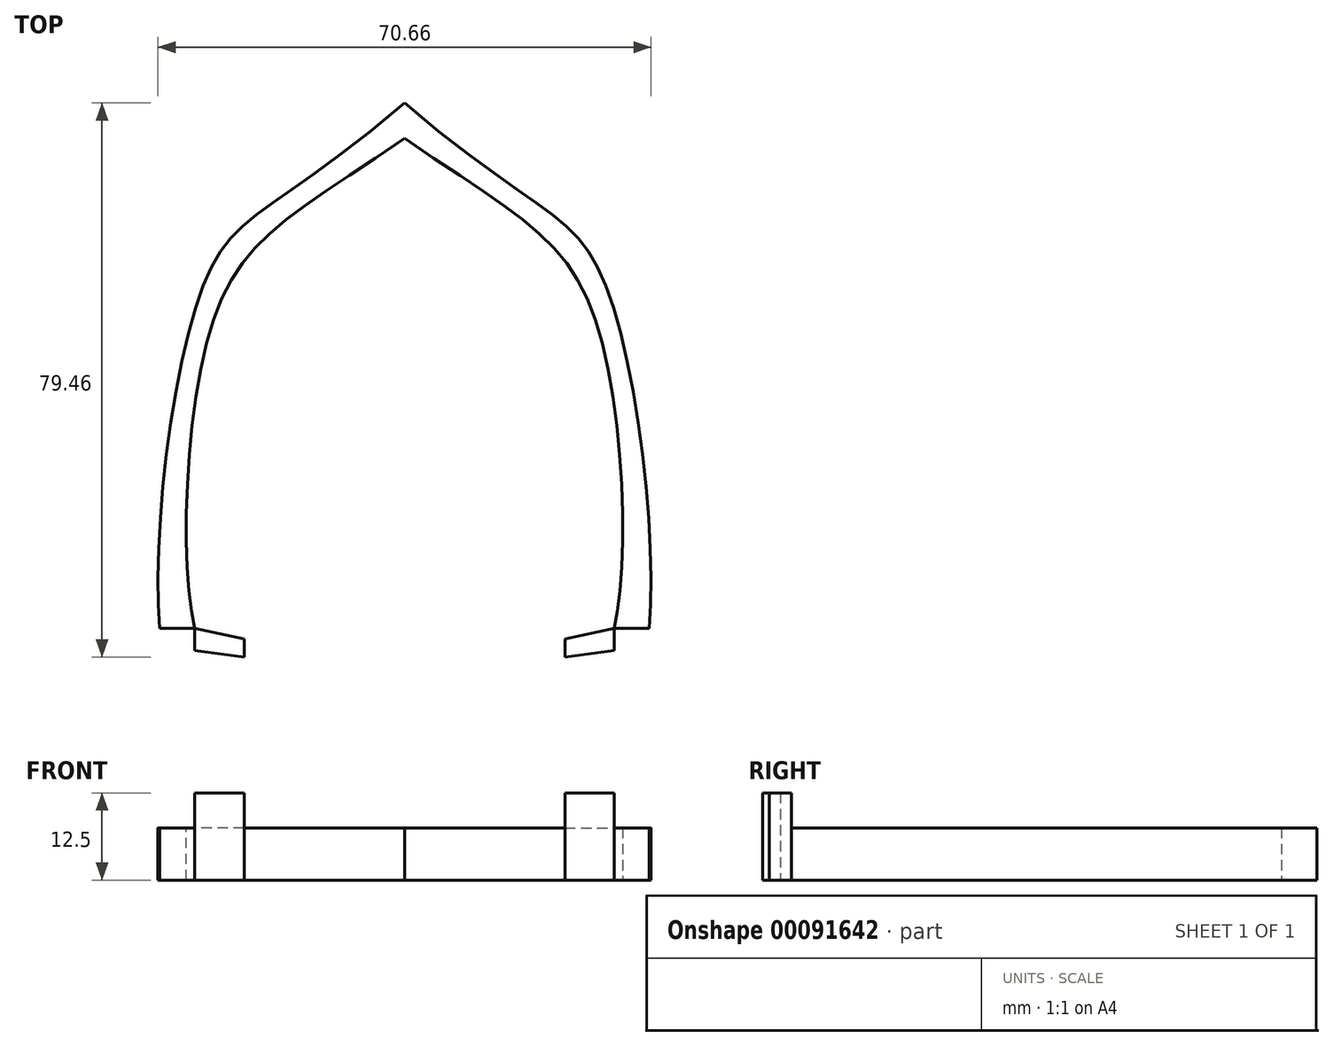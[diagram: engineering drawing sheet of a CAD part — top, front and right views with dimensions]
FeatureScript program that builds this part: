
annotation { "Feature Type Name" : "Feature", "Feature Type Description" : "" }
export const myFeature = defineFeature(function(context is Context, id is Id, definition is map)
    precondition{}
    {
        {
            var Q0;
            Q0=qCreatedBy(makeId("Top.planeOp"),FACE);
            var sketch = newSketch(context, id + "F0", { "sketchPlane" : qUnion([Q0])});
            skFitSpline(sketch, "E0", {"points": [v(0, 53.23) * mm, v(-28.51, 27.9) * mm, v(-35.06, -22.11) * mm], "startDerivative": vector(-121.37, -103.36) * mm, "endDerivative": vector(6.7, -73.45) * mm});
            skLineSegment(sketch, "E1", {"start": v(0, 53.23) * mm, "end": v(0, 48.14) * mm});
            skFitSpline(sketch, "E2", {"points": [v(0, 48.14) * mm, v(-27.4, 22.06) * mm, v(-30.06, -22.11) * mm], "startDerivative": vector(-100.93, -68.6) * mm, "endDerivative": vector(12.09, -49.62) * mm});
            skLineSegment(sketch, "E3", {"start": v(-30.06, -22.11) * mm, "end": v(-35.06, -22.11) * mm});
            skLineSegment(sketch, "E4.left", {"start": v(-30.06, -22.11) * mm, "end": v(-30.06, -27.16) * mm});
            skLineSegment(sketch, "E5.bottom", {"start": v(-35.06, -22.11) * mm, "end": v(-30.06, -22.11) * mm});
            skLineSegment(sketch, "E6", {"start": v(-30.06, -22.11) * mm, "end": v(-22.99, -23.66) * mm});
            skLineSegment(sketch, "E7", {"start": v(-22.99, -27.16) * mm, "end": v(-22.99, -23.66) * mm});
            skLineSegment(sketch, "E8", {"start": v(-22.99, -26.23) * mm, "end": v(-35.06, -24.63) * mm});
            skLineSegment(sketch, "E9", {"start": v(-35.06, -24.63) * mm, "end": v(-35.06, -22.11) * mm});
            skLineSegment(sketch, "E10.MirrorCS", {"start": v(30.06, -22.11) * mm, "end": v(35.06, -22.11) * mm});
            skLineSegment(sketch, "E11.MirrorCS", {"start": v(35.06, -22.11) * mm, "end": v(30.06, -22.11) * mm});
            skLineSegment(sketch, "E12.MirrorCS", {"start": v(35.06, -24.63) * mm, "end": v(35.06, -22.11) * mm});
            skLineSegment(sketch, "E13.MirrorCS", {"start": v(22.99, -27.16) * mm, "end": v(22.99, -23.66) * mm});
            skLineSegment(sketch, "E14.MirrorCS", {"start": v(30.06, -22.11) * mm, "end": v(30.06, -27.16) * mm});
            skLineSegment(sketch, "E15.MirrorCS", {"start": v(30.06, -22.11) * mm, "end": v(22.99, -23.66) * mm});
            skFitSpline(sketch, "E16.MirrorCS", {"points": [v(0, 53.23) * mm, v(28.51, 27.9) * mm, v(35.06, -22.11) * mm], "startDerivative": vector(121.37, -103.36) * mm, "endDerivative": vector(-6.7, -73.45) * mm});
            skLineSegment(sketch, "E17.MirrorCS", {"start": v(22.99, -26.23) * mm, "end": v(35.06, -24.63) * mm});
            skFitSpline(sketch, "E18.MirrorCS", {"points": [v(0, 48.14) * mm, v(27.4, 22.06) * mm, v(30.06, -22.11) * mm], "startDerivative": vector(100.93, -68.6) * mm, "endDerivative": vector(-12.09, -49.62) * mm});
            skSolve(sketch);
        }
        {
            var Q0;
            {var subQ0=sQuery(id+"F0.wireOp",EDGE,"E5.bottom");Q0=makeQuery(id+"F0.imprint","IMPRINT",FACE,{"disambiguationData":[TD([[makeQuery(id+"F0.imprint","IMPRINT",EDGE,{"derivedFrom":subQ0}),-1.0]])]});}
            var Q1;
            {var subQ0=sQuery(id+"F0.wireOp",EDGE,"E15.MirrorCS");Q1=makeQuery(id+"F0.imprint","IMPRINT",FACE,{"disambiguationData":[TD([[makeQuery(id+"F0.imprint","IMPRINT",EDGE,{"derivedFrom":subQ0}),1.0]])]});}
            var Q2;
            {var subQ0=sQuery(id+"F0.wireOp",EDGE,"E6");Q2=makeQuery(id+"F0.imprint","IMPRINT",FACE,{"disambiguationData":[TD([[makeQuery(id+"F0.imprint","IMPRINT",EDGE,{"derivedFrom":subQ0}),-1.0]])]});}
            var Q3;
            Q3=makeQuery(id+"F0.imprint","IMPRINT",FACE,{"disambiguationData":[TD([[makeQuery(id+"F0.imprint","IMPRINT",EDGE,{"derivedFrom":sQuery(id+"F0.wireOp",EDGE,"E0")}),1.0]])]});
            var Q4;
            Q4=makeQuery(id+"F0.imprint","IMPRINT",FACE,{"disambiguationData":[TD([[makeQuery(id+"F0.imprint","IMPRINT",EDGE,{"derivedFrom":sQuery(id+"F0.wireOp",EDGE,"E1")}),1.0]])]});
            var Q5;
            {var subQ0=sQuery(id+"F0.wireOp",EDGE,"E11.MirrorCS");Q5=makeQuery(id+"F0.imprint","IMPRINT",FACE,{"disambiguationData":[TD([[makeQuery(id+"F0.imprint","IMPRINT",EDGE,{"derivedFrom":subQ0}),1.0]])]});}
            extrude(context, id + "F1", {"entities" : qUnion([Q0, Q1, Q2, Q3, Q4, Q5]), "depth" : 7.5 * mm});
        }
        {
            var Q0;
            {var subQ0=sQuery(id+"F0.wireOp",EDGE,"E15.MirrorCS");Q0=makeQuery(id+"F0.imprint","IMPRINT",FACE,{"disambiguationData":[TD([[makeQuery(id+"F0.imprint","IMPRINT",EDGE,{"derivedFrom":subQ0}),1.0]])]});}
            extrude(context, id + "F2", {"entities" : qUnion([Q0]), "operationType" : NewBodyOperationType.ADD, "depth" : 12.5 * mm});
        }
        {
            var Q0;
            {var subQ0=sQuery(id+"F0.wireOp",EDGE,"E6");Q0=makeQuery(id+"F0.imprint","IMPRINT",FACE,{"disambiguationData":[TD([[makeQuery(id+"F0.imprint","IMPRINT",EDGE,{"derivedFrom":subQ0}),-1.0]])]});}
            extrude(context, id + "F3", {"entities" : qUnion([Q0]), "operationType" : NewBodyOperationType.ADD, "depth" : 12.5 * mm});
        }
    });
